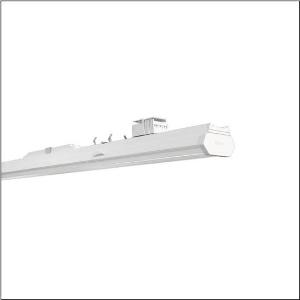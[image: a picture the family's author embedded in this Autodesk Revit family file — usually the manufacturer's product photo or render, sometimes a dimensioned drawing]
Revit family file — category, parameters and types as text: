
# Revit family: licross_11_protected_ho_51td13cn4e5s
name_source: partatom
category: Lighting Fixtures
units: mm (PartAtom-declared; Revit-internal decimal feet)

## family parameters
Cut with Voids When Loaded = No
Host = Face
Light Source = No
Part Type = Normal
Room Calculation Point = No
Round Connector Dimension = Use Diameter
Shared = No

## types (1)
- --- (1 x LED, 14500 lm, 77.6 W, 4000K)
    Apparent Load = 78 VA
    CIE Flux Codes = 89 96 99 100 99
    Color Rendering = 80
    Color Temperature = 4000K
    Default Elevation = 1800 mm
    Description = Licross 11 Protected HO, luminaire insert, of sheet steel, galvanised, coil coated, white, length: 1.500mm, width: 90mm, height: 101mm, LED rated luminous flux: 14.500lm, light colour: 840, SDCM (Standard Deviation of Colour Matching)MacAdam ≤ 2 SDCM (initial), control gear: ON/OFF Multilumen, CLOi, with plug, 3-pole, with phase selection, mains connection: 220..240V, AC, 50/60Hz, start of lifetime: 78W, end of service life: 87W, internal wiring halogen-free, primary light control with lens, of plastic, primary optical cover: cover, of PMMA, light emission: direct distribution, primary light characteristic: symmetric, protection rating (complete): IP54, insulation class (complete): insulation class I (protective earthing), certification: CE, ENEC, VDE, UKCA, protection symbol: D if used in an environment with non-conductive dust loads with corresponding accessories, impact resistance: IK06, permissible ambient temperature for indoor applications: -35..+35°C, corresponds to IFS (International Featured Standards) requirements for safety and quality in the food industry, reducing of maximum allowable ambient temperature of 5°C with ceiling mounting, LABS conformity tested according to VDMA 24364:2018-05, The light source and the operating device comply with the requirements of the Ecodesign Regulation (EU) 2019/2020 and are replaceable in accordance with this regulation, packaging unit: 1 piece
    Height = 92 mm
    Lamp = 1 x LED
    Lamp Light Flux = 14500 lm
    Lamp Power = 77.6 W
    Lamp count = 1
    Length = 1500 mm
    Luminous efficacy = 187 lm/W
    Manufacturer = Siteco
    ModVariant = No
    Model = 51TD13CN4E5S
    Mounting Place = Ceiling
    Mounting Type = Pendant
    Number of Poles = 1
    OnlyDefault = Yes
    Power Factor = 1
    Product Name = Licross 11 Protected HO
    Product group = luminaire insert | ceiling pendant
    ProductGroupID = 901
    Protection Class = Protection class I
    Protection Degree = IP 54
    RLX_Detail_Level = 1
    RLX_Emergency_Light_Flux = 0 lm
    RLX_Emergency_Type = 0
    RLX_Emergency_Type_DB = No
    RlxData = <blob elided: 22413 chars, md5=8426a788>
    Socket = socket
    Standby Power = 0 W
    System Light Flux = 14500 lm
    System Power = 78 W
    Type Comments = factory setting: luminous flux: 100 % | (A | C | E) | 181 mA
    Type Image = l_1256145.jpg
    URL = http://relux.com
    VarID = @adj_000649
    Voltage = 0 V
    Weight = 0.00 kg
    Width = 88 mm

## geometry (parser evidence)
native form markers: Blend x4, Sweep x11
no freeform markers — native parametric forms only
